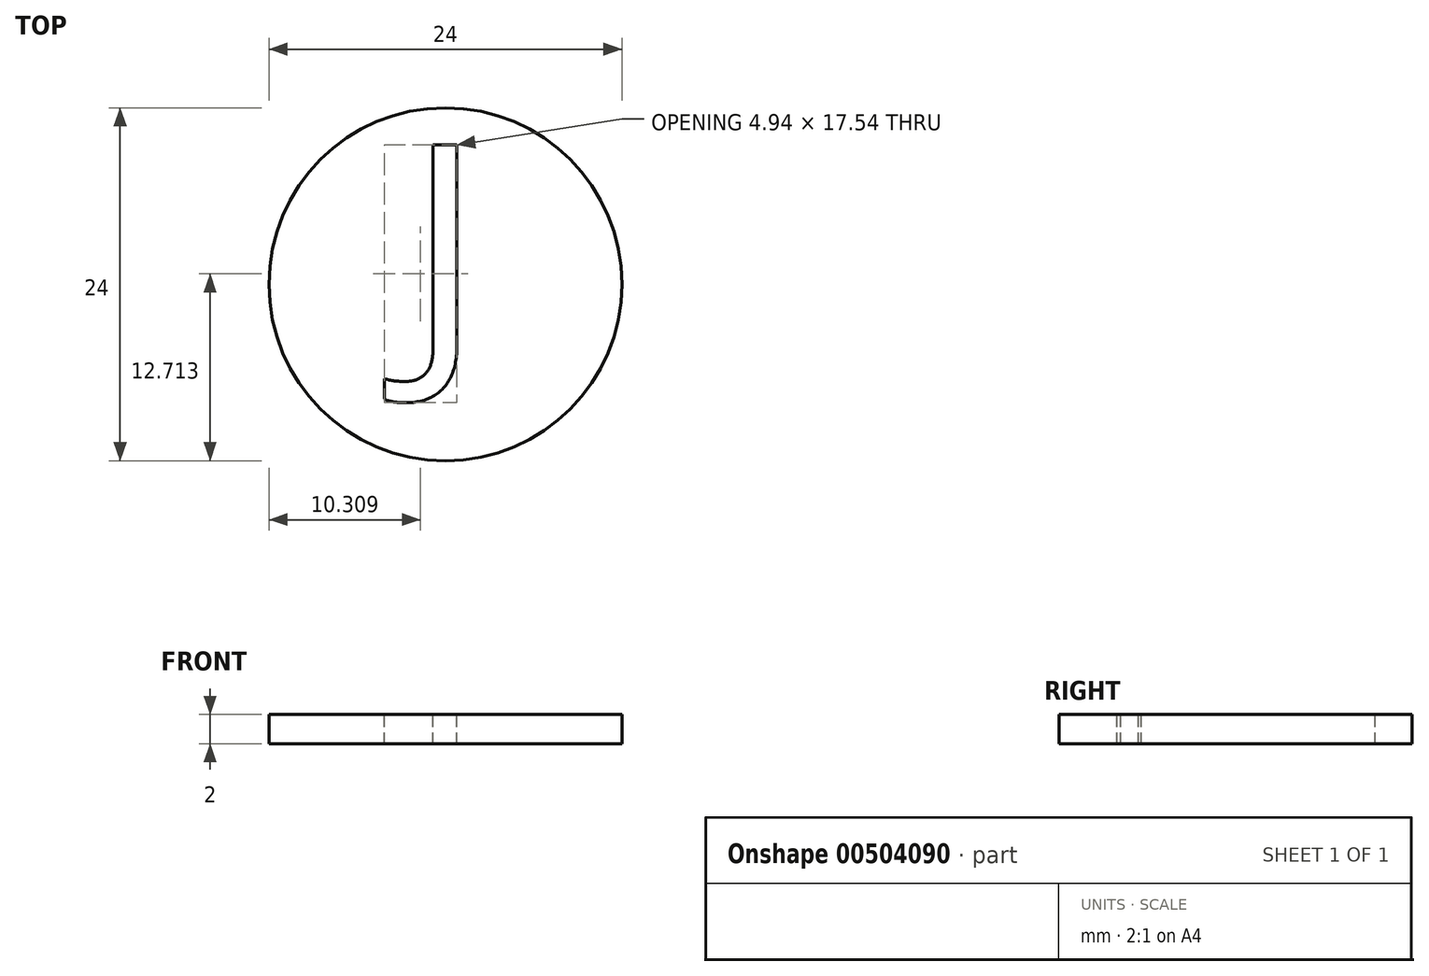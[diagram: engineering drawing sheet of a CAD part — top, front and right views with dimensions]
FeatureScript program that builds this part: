
annotation { "Feature Type Name" : "Feature", "Feature Type Description" : "" }
export const myFeature = defineFeature(function(context is Context, id is Id, definition is map)
    precondition{}
    {
        {
            var Q0;
            Q0=qCreatedBy(makeId("Top.planeOp"),FACE);
            var sketch = newSketch(context, id + "F0", { "sketchPlane" : qUnion([Q0])});
            skCircle(sketch, "E0", {"center": v(0, 0) * mm, "radius": 12 * mm});
            skSolve(sketch);
        }
        {
            var Q0;
            Q0=qSketchRegion(id+"F0",true);
            extrude(context, id + "F1", {"entities" : qUnion([Q0]), "depth" : 2 * mm});
        }
        {
            var Q0;
            Q0=makeQuery(id+"F1.opExtrude","CAP_FACE",FACE,{"disambiguationData":[OSD([sQuery(id+"F0.wireOp",EDGE,"E0")])],"isStart":false});
            var sketch = newSketch(context, id + "F2", { "sketchPlane" : qUnion([Q0])});
            skPoint(sketch, "E1", {"position": v(0, 12) * mm});
            skText(sketch, "E2", { "text": "J", "fontName": "OpenSans-Regular.ttf"});
            const initialGuessF2  = {"E2": [-0.00264, -0.0044, 1, 0, 0.014]};
            skSetInitialGuess(sketch, initialGuessF2);
            skSolve(sketch);
        }
        {
            var Q0;
            Q0 = qSketchRegion(id + "F2", true);
            extrude(context, id + "F3", {"entities" : qUnion([Q0]), "operationType" : NewBodyOperationType.REMOVE, "oppositeDirection" : true, "depth" : 25 * mm});
        }
    });
